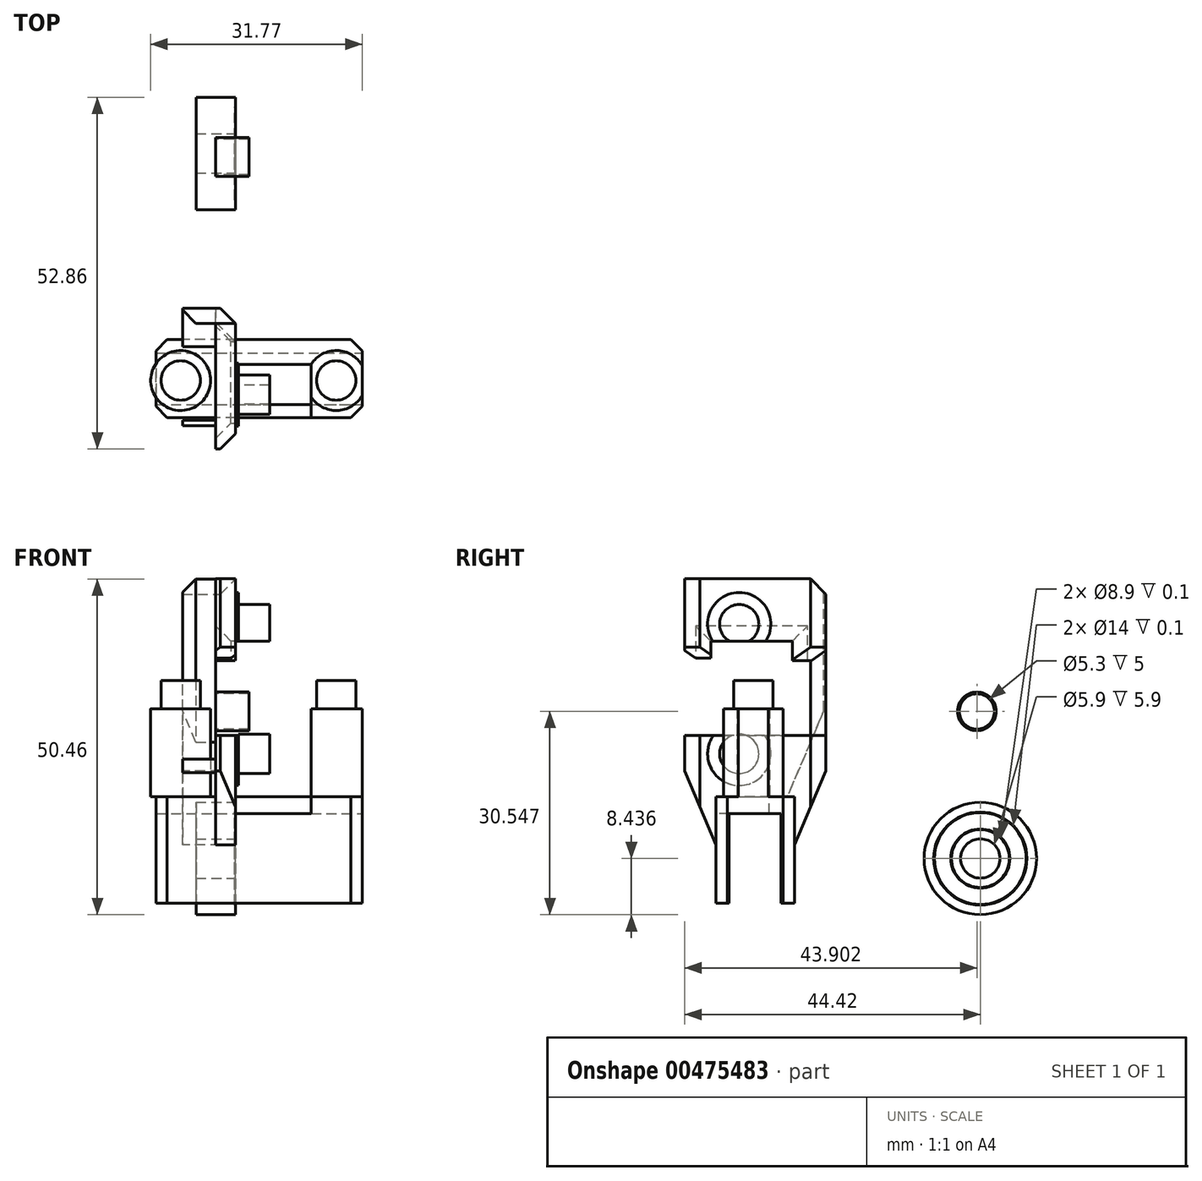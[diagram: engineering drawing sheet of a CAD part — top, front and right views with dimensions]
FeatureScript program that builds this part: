
annotation { "Feature Type Name" : "Feature", "Feature Type Description" : "" }
export const myFeature = defineFeature(function(context is Context, id is Id, definition is map)
    precondition{}
    {
        {
            var Q0;
            Q0=qCreatedBy(makeId("Right.planeOp"),FACE);
            var sketch = newSketch(context, id + "F0", { "sketchPlane" : qUnion([Q0])});
            skLineSegment(sketch, "E0", {"start": v(16.47, 8.85) * mm, "end": v(16.47, -7.15) * mm});
            skLineSegment(sketch, "E1", {"start": v(16.47, -7.15) * mm, "end": v(14.47, -7.15) * mm});
            skLineSegment(sketch, "E2", {"start": v(14.47, -7.15) * mm, "end": v(14.47, 6.35) * mm});
            skLineSegment(sketch, "E3", {"start": v(6.67, 6.35) * mm, "end": v(6.67, -7.15) * mm});
            skLineSegment(sketch, "E4", {"start": v(4.71, -7.15) * mm, "end": v(4.71, 8.85) * mm});
            skLineSegment(sketch, "E5", {"start": v(4.71, 8.85) * mm, "end": v(16.47, 8.85) * mm});
            skLineSegment(sketch, "E6.trimOffspring", {"start": v(14.47, 6.35) * mm, "end": v(6.67, 6.35) * mm});
            skLineSegment(sketch, "E7.trimOffspring", {"start": v(6.67, -7.15) * mm, "end": v(4.71, -7.15) * mm});
            skCircle(sketch, "E8", {"center": v(44.42, -0.43) * mm, "radius": 8.44 * mm});
            skCircle(sketch, "E9", {"center": v(44.42, -0.43) * mm, "radius": 2.95 * mm});
            skLineSegment(sketch, "E10", {"start": v(0, 41.6) * mm, "end": v(21.19, 41.6) * mm});
            skLineSegment(sketch, "E11", {"start": v(3.93, 21.47) * mm, "end": v(16.17, 21.47) * mm});
            skLineSegment(sketch, "E12", {"start": v(16.17, 21.47) * mm, "end": v(16.17, 32.21) * mm});
            skLineSegment(sketch, "E13", {"start": v(0, 41.6) * mm, "end": v(0, 12.74) * mm});
            skLineSegment(sketch, "E14", {"start": v(3.93, 32.21) * mm, "end": v(3.93, 21.47) * mm});
            skLineSegment(sketch, "E15", {"start": v(0, 12.74) * mm, "end": v(4.71, 1.64) * mm});
            skCircle(sketch, "E16", {"center": v(44.42, -0.43) * mm, "radius": 4.35 * mm});
            skCircle(sketch, "E17", {"center": v(44.42, -0.43) * mm, "radius": 4.45 * mm});
            skCircle(sketch, "E18", {"center": v(44.42, -0.43) * mm, "radius": 7 * mm});
            skCircle(sketch, "E19", {"center": v(44.42, -0.43) * mm, "radius": 6.9 * mm});
            skLineSegment(sketch, "E20", {"start": v(3.93, 32.21) * mm, "end": v(16.17, 32.21) * mm});
            skLineSegment(sketch, "E21", {"start": v(16.47, 1.64) * mm, "end": v(21.19, 12.74) * mm});
            skLineSegment(sketch, "E22", {"start": v(21.19, 12.74) * mm, "end": v(21.19, 41.6) * mm});
            skCircle(sketch, "E23.0", {"center": v(8.2, 15.3) * mm, "radius": 2.95 * mm});
            skArc(sketch, "E23.1", {"start": v(9.6, 32.21) * mm, "mid": v(8.2, 37.75) * mm, "end": v(6.78, 32.21) * mm});
            skArc(sketch, "E24", {"start": v(12.17, 32.21) * mm, "mid": v(8.2, 39.55) * mm, "end": v(4.2, 32.21) * mm});
            skArc(sketch, "E25", {"start": v(3.5, 14.5) * mm, "mid": v(12.87, 16.1) * mm, "end": v(3.5, 14.51) * mm});
            skLineSegment(sketch, "E26", {"start": v(1.75, 41.6) * mm, "end": v(1.75, 18.64) * mm});
            skLineSegment(sketch, "E27", {"start": v(18.9, 41.6) * mm, "end": v(18.9, 17.06) * mm});
            skLineSegment(sketch, "E28", {"start": v(18.9, 17.06) * mm, "end": v(15.4, 8.85) * mm});
            skLineSegment(sketch, "E29", {"start": v(1.75, 18.64) * mm, "end": v(5.91, 8.85) * mm});
            skCircle(sketch, "E30", {"center": v(43.9, 21.68) * mm, "radius": 2.65 * mm});
            skCircle(sketch, "E31", {"center": v(43.9, 21.68) * mm, "radius": 2.9 * mm});
            skLineSegment(sketch, "E32", {"start": v(3.5, 14.51) * mm, "end": v(3.5, 14.5) * mm});
            skSolve(sketch);
        }
        {
            var Q0;
            Q0=makeQuery(id+"F0.imprint","IMPRINT",FACE,{"disambiguationData":[TD([[makeQuery(id+"F0.imprint","IMPRINT",EDGE,{"derivedFrom":sQuery(id+"F0.wireOp",EDGE,"E0")}),-1.0]])]});
            extrude(context, id + "F1", {"entities" : qUnion([Q0]), "oppositeDirection" : true, "depth" : 9 * mm, "offsetDistance" : 25 * mm});
        }
        {
            var Q0;
            Q0=makeQuery(id+"F0.imprint","IMPRINT",FACE,{"disambiguationData":[TD([[makeQuery(id+"F0.imprint","IMPRINT",EDGE,{"derivedFrom":sQuery(id+"F0.wireOp",EDGE,"E0")}),-1.0]])]});
            extrude(context, id + "F2", {"entities" : qUnion([Q0]), "operationType" : NewBodyOperationType.ADD, "depth" : 22 * mm, "offsetDistance" : 25 * mm});
        }
        {
            var Q0;
            Q0=makeQuery(id+"F0.imprint","IMPRINT",FACE,{"disambiguationData":[TD([[makeQuery(id+"F0.imprint","IMPRINT",EDGE,{"derivedFrom":sQuery(id+"F0.wireOp",EDGE,"E4")}),1.0]])]});
            var Q1;
            {var subQ0=sQuery(id+"F0.wireOp",EDGE,"E24");Q1=makeQuery(id+"F0.imprint","IMPRINT",FACE,{"disambiguationData":[TD([[makeQuery(id+"F0.imprint","IMPRINT",EDGE,{"derivedFrom":subQ0}),1.0]])]});}
            var Q2;
            Q2=makeQuery(id+"F0.imprint","IMPRINT",FACE,{"disambiguationData":[TD([[makeQuery(id+"F0.imprint","IMPRINT",EDGE,{"derivedFrom":sQuery(id+"F0.wireOp",EDGE,"E23.0")}),-1.0]])]});
            var Q3;
            {var subQ5=sQuery(id+"F0.wireOp",EDGE,"N7SW8Tvq-peLj-d8hC-b9Bx-wYODAvh42Vg8");Q3=makeQuery(id+"F0.imprint","IMPRINT",FACE,{"disambiguationData":[TD([[makeQuery(id+"F0.imprint","IMPRINT",EDGE,{"derivedFrom":subQ5}),1.0]])]});}
            var Q4;
            {var subQ5=sQuery(id+"F0.wireOp",EDGE,"2wB0xuDN-6za4-80fk-EIJ2-dwkkp9VSf7dO");Q4=makeQuery(id+"F0.imprint","IMPRINT",FACE,{"disambiguationData":[TD([[makeQuery(id+"F0.imprint","IMPRINT",EDGE,{"derivedFrom":subQ5}),-1.0]])]});}
            var Q5;
            {var subQ3=sQuery(id+"F0.wireOp",EDGE,"1ilUMg3S-6E9J-L5an-a0RG-rZSRoxiEg0z6");Q5=makeQuery(id+"F0.imprint","IMPRINT",FACE,{"disambiguationData":[TD([[makeQuery(id+"F0.imprint","IMPRINT",EDGE,{"derivedFrom":subQ3}),1.0]])]});}
            var Q6;
            {var subQ5=sQuery(id+"F0.wireOp",EDGE,"BMftJzpG-nXOZ-MVrK-hpTt-UoZ4K3T9nTGc");Q6=makeQuery(id+"F0.imprint","IMPRINT",FACE,{"disambiguationData":[TD([[makeQuery(id+"F0.imprint","IMPRINT",EDGE,{"derivedFrom":subQ5}),-1.0]])]});}
            var Q7;
            {var subQ0=sQuery(id+"F0.wireOp",EDGE,"E22");Q7=makeQuery(id+"F0.imprint","IMPRINT",FACE,{"disambiguationData":[TD([[makeQuery(id+"F0.imprint","IMPRINT",EDGE,{"derivedFrom":subQ0}),1.0]])]});}
            var Q8;
            {var subQ0=sQuery(id+"F0.wireOp",EDGE,"E13");Q8=makeQuery(id+"F0.imprint","IMPRINT",FACE,{"disambiguationData":[TD([[makeQuery(id+"F0.imprint","IMPRINT",EDGE,{"derivedFrom":subQ0}),1.0]])]});}
            var Q9;
            Q9=makeQuery(id+"F0.imprint","IMPRINT",FACE,{"disambiguationData":[TD([[makeQuery(id+"F0.imprint","IMPRINT",EDGE,{"derivedFrom":sQuery(id+"F0.wireOp",EDGE,"E11")}),-1.0]])]});
            var Q10;
            {var subQ0=sQuery(id+"F0.wireOp",EDGE,"E32");Q10=makeQuery(id+"F0.imprint","IMPRINT",FACE,{"disambiguationData":[TD([[makeQuery(id+"F0.imprint","IMPRINT",EDGE,{"derivedFrom":subQ0}),1.0]])]});}
            extrude(context, id + "F3", {"entities" : qUnion([Q0, Q1, Q2, Q3, Q4, Q5, Q6, Q7, Q8, Q9, Q10]), "operationType" : NewBodyOperationType.ADD, "depth" : 3 * mm, "offsetDistance" : 25 * mm});
        }
        {
            var Q0;
            {var subQ0=sQuery(id+"F0.wireOp",EDGE,"E13");Q0=makeQuery(id+"F0.imprint","IMPRINT",FACE,{"disambiguationData":[TD([[makeQuery(id+"F0.imprint","IMPRINT",EDGE,{"derivedFrom":subQ0}),1.0]])]});}
            var Q1;
            {var subQ0=sQuery(id+"F0.wireOp",EDGE,"E22");Q1=makeQuery(id+"F0.imprint","IMPRINT",FACE,{"disambiguationData":[TD([[makeQuery(id+"F0.imprint","IMPRINT",EDGE,{"derivedFrom":subQ0}),1.0]])]});}
            var Q2;
            {var subQ0=sQuery(id+"F0.wireOp",EDGE,"E32");Q2=makeQuery(id+"F0.imprint","IMPRINT",FACE,{"disambiguationData":[TD([[makeQuery(id+"F0.imprint","IMPRINT",EDGE,{"derivedFrom":subQ0}),1.0]])]});}
            extrude(context, id + "F4", {"entities" : qUnion([Q0, Q1, Q2]), "operationType" : NewBodyOperationType.ADD, "oppositeDirection" : true, "depth" : 5 * mm, "offsetDistance" : 25 * mm});
        }
        {
            var Q0;
            Q0=makeQuery(id+"F0.imprint","IMPRINT",FACE,{"disambiguationData":[TD([[makeQuery(id+"F0.imprint","IMPRINT",EDGE,{"derivedFrom":sQuery(id+"F0.wireOp",EDGE,"7a95fe76-a82b-47bc-b71d-d71758565e7d.1")}),1.0]])]});
            var Q1;
            Q1=makeQuery(id+"F0.imprint","IMPRINT",FACE,{"disambiguationData":[TD([[makeQuery(id+"F0.imprint","IMPRINT",EDGE,{"derivedFrom":sQuery(id+"F0.wireOp",EDGE,"4c5e037e-bfb9-4179-b28a-ed57e4a18d11.1")}),1.0]])]});
            var Q2;
            Q2=makeQuery(id+"F0.imprint","IMPRINT",FACE,{"disambiguationData":[TD([[makeQuery(id+"F0.imprint","IMPRINT",EDGE,{"derivedFrom":sQuery(id+"F0.wireOp",EDGE,"E23.0")}),1.0]])]});
            var Q3;
            {var subQ0=sQuery(id+"F0.wireOp",EDGE,"E23.1");Q3=makeQuery(id+"F0.imprint","IMPRINT",FACE,{"disambiguationData":[TD([[makeQuery(id+"F0.imprint","IMPRINT",EDGE,{"derivedFrom":subQ0}),1.0]])]});}
            extrude(context, id + "F5", {"entities" : qUnion([Q0, Q1, Q2, Q3]), "operationType" : NewBodyOperationType.ADD, "depth" : 8.1 * mm, "offsetDistance" : 25 * mm});
        }
        {
            var Q0;
            {var subQ0=sQuery(id+"F0.wireOp",EDGE,"E24");Q0=makeQuery(id+"F0.imprint","IMPRINT",FACE,{"disambiguationData":[TD([[makeQuery(id+"F0.imprint","IMPRINT",EDGE,{"derivedFrom":subQ0}),1.0]])]});}
            var Q1;
            Q1=makeQuery(id+"F0.imprint","IMPRINT",FACE,{"disambiguationData":[TD([[makeQuery(id+"F0.imprint","IMPRINT",EDGE,{"derivedFrom":sQuery(id+"F0.wireOp",EDGE,"E23.0")}),-1.0]])]});
            var Q2;
            {var subQ0=sQuery(id+"F0.wireOp",EDGE,"E32");Q2=makeQuery(id+"F0.imprint","IMPRINT",FACE,{"disambiguationData":[TD([[makeQuery(id+"F0.imprint","IMPRINT",EDGE,{"derivedFrom":subQ0}),1.0]])]});}
            extrude(context, id + "F6", {"entities" : qUnion([Q0, Q1, Q2]), "operationType" : NewBodyOperationType.ADD, "depth" : 3.4 * mm, "offsetDistance" : 25 * mm});
        }
        {
            var Q0;
            {var subQ0=sQuery(id+"F0.wireOp",EDGE,"E0");var subQ1=sQuery(id+"F0.wireOp",EDGE,"E4");var subQ3=sQuery(id+"F0.wireOp",EDGE,"E5");Q0=makeQuery(id+"F3.boolean.opBoolean","SPLIT",FACE,{"disambiguationData":[TD([makeQuery(id+"F1.opExtrude","CAP_FACE",FACE,{"disambiguationData":[OSD([subQ0,sQuery(id+"F0.wireOp",EDGE,"E1"),sQuery(id+"F0.wireOp",EDGE,"E2"),sQuery(id+"F0.wireOp",EDGE,"E3"),subQ1,subQ3,sQuery(id+"F0.wireOp",EDGE,"E6.trimOffspring"),sQuery(id+"F0.wireOp",EDGE,"E7.trimOffspring")])],"isStart":false})])],"derivedFrom":makeQuery(id+"F2.boolean.opBoolean","MERGE",FACE,{"derivedFrom":[makeQuery(id+"F1.opExtrude","SWEPT_FACE",FACE,{"disambiguationData":[OSD([subQ3])]}),makeQuery(id+"F2.opExtrude","SWEPT_FACE",FACE,{"disambiguationData":[OSD([subQ3])]})]})});}
            var sketch = newSketch(context, id + "F7", { "sketchPlane" : qUnion([Q0])});
            skCircle(sketch, "E33.0", {"center": v(-5.27, 10.3) * mm, "radius": 2.96 * mm});
            skCircle(sketch, "E33.1", {"center": v(18.1, 10.3) * mm, "radius": 2.96 * mm});
            skCircle(sketch, "E34", {"center": v(-5.27, 10.3) * mm, "radius": 4.5 * mm});
            skArc(sketch, "E35", {"start": v(22, 12.55) * mm, "mid": v(13.6, 10.3) * mm, "end": v(22, 8.07) * mm});
            skLineSegment(sketch, "E36.0", {"start": v(22, 8.07) * mm, "end": v(22, 12.55) * mm});
            skPoint(sketch, "E37.orphan", {"position": v(22, 16.47) * mm});
            skPoint(sketch, "E38.orphan", {"position": v(22, 4.71) * mm});
            skSolve(sketch);
        }
        {
            var Q0;
            {var subQ0=sQuery(id+"F7.wireOp",EDGE,"006e9b06-de1a-4e6b-b88b-39552be878e9.0");var subQ1=sQuery(id+"F0.wireOp",EDGE,"E4");var subQ2=sQuery(id+"F0.wireOp",EDGE,"E5");var subQ3=makeQuery(id+"F3.boolean.opBoolean","SPLIT",EDGE,{"disambiguationData":[TD([makeQuery(id+"F1.opExtrude","CAP_FACE",FACE,{"disambiguationData":[OSD([sQuery(id+"F0.wireOp",EDGE,"E0"),sQuery(id+"F0.wireOp",EDGE,"E1"),sQuery(id+"F0.wireOp",EDGE,"E2"),sQuery(id+"F0.wireOp",EDGE,"E3"),subQ1,subQ2,sQuery(id+"F0.wireOp",EDGE,"E6.trimOffspring"),sQuery(id+"F0.wireOp",EDGE,"E7.trimOffspring")])],"isStart":false})])],"derivedFrom":makeQuery(id+"F2.boolean.opBoolean","MERGE",EDGE,{"derivedFrom":[makeQuery(id+"F1.opExtrude","SWEPT_EDGE",EDGE,{"disambiguationData":[OSD([subQ1,subQ2])]}),makeQuery(id+"F2.opExtrude","SWEPT_EDGE",EDGE,{"disambiguationData":[OSD([subQ1,subQ2])]})]})});var subQ4=makeQuery(id+"F7.imprint","INTERSECT",VERTEX,{"disambiguationData":[OD(0.0)],"derivedFrom":[subQ3,subQ0]});Q0=makeQuery(id+"F7.imprint","IMPRINT",FACE,{"disambiguationData":[TD([[makeQuery(id+"F7.imprint","IMPRINT",EDGE,{"disambiguationData":[TD([[subQ4,-1.0]])],"derivedFrom":subQ0}),-1.0]])]});}
            var Q1;
            {var subQ0=sQuery(id+"F7.wireOp",EDGE,"scUp9ceF-Qq33-h5mQ-G7V0-FORdipvKPfS7");var subQ1=sQuery(id+"F7.wireOp",EDGE,"006e9b06-de1a-4e6b-b88b-39552be878e9.0");var subQ2=makeQuery(id+"F7.imprint","INTERSECT",VERTEX,{"disambiguationData":[OD(0.0)],"derivedFrom":[subQ1,subQ0]});Q1=makeQuery(id+"F7.imprint","IMPRINT",FACE,{"disambiguationData":[TD([[makeQuery(id+"F7.imprint","IMPRINT",EDGE,{"disambiguationData":[TD([[subQ2,-1.0]])],"derivedFrom":subQ0}),1.0]])]});}
            var Q2;
            Q2=makeQuery(id+"F7.imprint","IMPRINT",FACE,{"disambiguationData":[TD([[makeQuery(id+"F7.imprint","IMPRINT",EDGE,{"derivedFrom":sQuery(id+"F7.wireOp",EDGE,"006e9b06-de1a-4e6b-b88b-39552be878e9.1")}),-1.0]])]});
            var Q3;
            Q3=makeQuery(id+"F7.imprint","IMPRINT",FACE,{"disambiguationData":[TD([[makeQuery(id+"F7.imprint","IMPRINT",EDGE,{"derivedFrom":sQuery(id+"F7.wireOp",EDGE,"E33.0")}),1.0]])]});
            var Q4;
            Q4=makeQuery(id+"F7.imprint","IMPRINT",FACE,{"disambiguationData":[TD([[makeQuery(id+"F7.imprint","IMPRINT",EDGE,{"derivedFrom":sQuery(id+"F7.wireOp",EDGE,"E33.1")}),1.0]])]});
            extrude(context, id + "F8", {"entities" : qUnion([Q0, Q1, Q2, Q3, Q4]), "operationType" : NewBodyOperationType.ADD, "depth" : 17.5 * mm, "offsetDistance" : 25 * mm});
        }
        {
            var Q0;
            {var subQ0=sQuery(id+"F7.wireOp",EDGE,"scUp9ceF-Qq33-h5mQ-G7V0-FORdipvKPfS7");var subQ1=sQuery(id+"F7.wireOp",EDGE,"006e9b06-de1a-4e6b-b88b-39552be878e9.0");var subQ2=makeQuery(id+"F7.imprint","INTERSECT",VERTEX,{"disambiguationData":[OD(1.0)],"derivedFrom":[subQ1,subQ0]});Q0=makeQuery(id+"F7.imprint","IMPRINT",FACE,{"disambiguationData":[TD([[makeQuery(id+"F7.imprint","IMPRINT",EDGE,{"disambiguationData":[TD([[subQ2,-1.0]])],"derivedFrom":subQ0}),1.0]])]});}
            var Q1;
            {var subQ0=sQuery(id+"F7.wireOp",EDGE,"scUp9ceF-Qq33-h5mQ-G7V0-FORdipvKPfS7");var subQ1=sQuery(id+"F7.wireOp",EDGE,"006e9b06-de1a-4e6b-b88b-39552be878e9.0");var subQ2=makeQuery(id+"F7.imprint","INTERSECT",VERTEX,{"disambiguationData":[OD(0.0)],"derivedFrom":[subQ1,subQ0]});Q1=makeQuery(id+"F7.imprint","IMPRINT",FACE,{"disambiguationData":[TD([[makeQuery(id+"F7.imprint","IMPRINT",EDGE,{"disambiguationData":[TD([[subQ2,1.0]])],"derivedFrom":subQ0}),1.0]])]});}
            var Q2;
            {var subQ0=sQuery(id+"F7.wireOp",EDGE,"006e9b06-de1a-4e6b-b88b-39552be878e9.0");var subQ1=sQuery(id+"F0.wireOp",EDGE,"E4");var subQ2=sQuery(id+"F0.wireOp",EDGE,"E5");var subQ3=makeQuery(id+"F3.boolean.opBoolean","SPLIT",EDGE,{"disambiguationData":[TD([makeQuery(id+"F1.opExtrude","CAP_FACE",FACE,{"disambiguationData":[OSD([sQuery(id+"F0.wireOp",EDGE,"E0"),sQuery(id+"F0.wireOp",EDGE,"E1"),sQuery(id+"F0.wireOp",EDGE,"E2"),sQuery(id+"F0.wireOp",EDGE,"E3"),subQ1,subQ2,sQuery(id+"F0.wireOp",EDGE,"E6.trimOffspring"),sQuery(id+"F0.wireOp",EDGE,"E7.trimOffspring")])],"isStart":false})])],"derivedFrom":makeQuery(id+"F2.boolean.opBoolean","MERGE",EDGE,{"derivedFrom":[makeQuery(id+"F1.opExtrude","SWEPT_EDGE",EDGE,{"disambiguationData":[OSD([subQ1,subQ2])]}),makeQuery(id+"F2.opExtrude","SWEPT_EDGE",EDGE,{"disambiguationData":[OSD([subQ1,subQ2])]})]})});var subQ4=makeQuery(id+"F7.imprint","INTERSECT",VERTEX,{"disambiguationData":[OD(0.0)],"derivedFrom":[subQ3,subQ0]});Q2=makeQuery(id+"F7.imprint","IMPRINT",FACE,{"disambiguationData":[TD([[makeQuery(id+"F7.imprint","IMPRINT",EDGE,{"disambiguationData":[TD([[subQ4,-1.0]])],"derivedFrom":subQ0}),1.0]])]});}
            var Q3;
            Q3=makeQuery(id+"F7.imprint","IMPRINT",FACE,{"disambiguationData":[TD([[makeQuery(id+"F7.imprint","IMPRINT",EDGE,{"derivedFrom":sQuery(id+"F7.wireOp",EDGE,"006e9b06-de1a-4e6b-b88b-39552be878e9.1")}),1.0]])]});
            var Q4;
            Q4=makeQuery(id+"F7.imprint","IMPRINT",FACE,{"disambiguationData":[TD([[makeQuery(id+"F7.imprint","IMPRINT",EDGE,{"derivedFrom":sQuery(id+"F7.wireOp",EDGE,"E33.0")}),-1.0]])]});
            var Q5;
            Q5=makeQuery(id+"F7.imprint","IMPRINT",FACE,{"disambiguationData":[TD([[makeQuery(id+"F7.imprint","IMPRINT",EDGE,{"derivedFrom":sQuery(id+"F7.wireOp",EDGE,"E33.1")}),-1.0]])]});
            var Q6;
            {var subQ0=sQuery(id+"F7.wireOp",EDGE,"E34");var subQ1=sQuery(id+"F0.wireOp",EDGE,"E5");var subQ2=sQuery(id+"F0.wireOp",EDGE,"E29");var subQ5=makeQuery(id+"F4.opExtrude","SWEPT_EDGE",EDGE,{"disambiguationData":[OSD([subQ1,subQ2])]});var subQ6=makeQuery(id+"F7.imprint","INTERSECT",VERTEX,{"derivedFrom":[subQ5,subQ0]});Q6=makeQuery(id+"F7.imprint","IMPRINT",FACE,{"disambiguationData":[TD([[makeQuery(id+"F7.imprint","IMPRINT",EDGE,{"disambiguationData":[TD([[subQ6,1.0]])],"derivedFrom":subQ0}),1.0]])]});}
            extrude(context, id + "F9", {"entities" : qUnion([Q0, Q1, Q2, Q3, Q4, Q5, Q6]), "operationType" : NewBodyOperationType.ADD, "depth" : 13.23 * mm, "offsetDistance" : 25 * mm});
        }
        {
            var Q0;
            {var subQ0=sQuery(id+"F0.wireOp",EDGE,"E5");var subQ1=sQuery(id+"F0.wireOp",EDGE,"E7.trimOffspring");var subQ2=sQuery(id+"F0.wireOp",EDGE,"E4");Q0=makeQuery(id+"F3.boolean.opBoolean","SPLIT",FACE,{"disambiguationData":[TD([makeQuery(id+"F2.opExtrude","CAP_FACE",FACE,{"disambiguationData":[OSD([sQuery(id+"F0.wireOp",EDGE,"E0"),sQuery(id+"F0.wireOp",EDGE,"E1"),sQuery(id+"F0.wireOp",EDGE,"E2"),sQuery(id+"F0.wireOp",EDGE,"E3"),subQ2,subQ0,sQuery(id+"F0.wireOp",EDGE,"E6.trimOffspring"),subQ1])],"isStart":false})])],"derivedFrom":makeQuery(id+"F2.boolean.opBoolean","MERGE",FACE,{"derivedFrom":[makeQuery(id+"F1.opExtrude","SWEPT_FACE",FACE,{"disambiguationData":[OSD([subQ2])]}),makeQuery(id+"F2.opExtrude","SWEPT_FACE",FACE,{"disambiguationData":[OSD([subQ2])]})]})});}
            var sketch = newSketch(context, id + "F10", { "sketchPlane" : qUnion([Q0])});
            skLineSegment(sketch, "E39", {"start": v(3, 8.85) * mm, "end": v(3, 6.34) * mm});
            skLineSegment(sketch, "E40", {"start": v(3, 6.34) * mm, "end": v(14.33, 6.34) * mm});
            skLineSegment(sketch, "E41", {"start": v(14.33, 6.34) * mm, "end": v(14.33, 8.85) * mm});
            skLineSegment(sketch, "E42", {"start": v(14.33, 8.85) * mm, "end": v(3, 8.85) * mm});
            skPoint(sketch, "E43.0", {"position": v(3, 41.6) * mm});
            skLineSegment(sketch, "E44.bottom", {"start": v(0, 29.33) * mm, "end": v(3.44, 29.33) * mm});
            skLineSegment(sketch, "E44.top", {"start": v(0, 18.05) * mm, "end": v(3.44, 18.05) * mm});
            skLineSegment(sketch, "E44.left", {"start": v(0, 29.33) * mm, "end": v(0, 18.05) * mm});
            skLineSegment(sketch, "E44.right", {"start": v(3.44, 29.33) * mm, "end": v(3.44, 18.05) * mm});
            skLineSegment(sketch, "E45.bottom", {"start": v(12.56, 23.46) * mm, "end": v(14.33, 23.46) * mm});
            skLineSegment(sketch, "E45.top", {"start": v(12.56, 8.85) * mm, "end": v(14.33, 8.85) * mm});
            skLineSegment(sketch, "E45.left", {"start": v(12.56, 23.46) * mm, "end": v(12.56, 8.85) * mm});
            skLineSegment(sketch, "E45.right", {"start": v(14.33, 23.46) * mm, "end": v(14.33, 8.85) * mm});
            skSolve(sketch);
        }
        {
            var Q0;
            Q0=makeQuery(id+"F10.imprint","IMPRINT",FACE,{"disambiguationData":[TD([[makeQuery(id+"F10.imprint","IMPRINT",EDGE,{"derivedFrom":sQuery(id+"F10.wireOp",EDGE,"E39")}),-1.0]])]});
            extrude(context, id + "F11", {"entities" : qUnion([Q0]), "operationType" : NewBodyOperationType.REMOVE, "oppositeDirection" : true, "depth" : 8 * mm, "offsetDistance" : 25 * mm});
        }
        {
            var Q0;
            Q0=makeQuery(id+"F10.imprint","IMPRINT",FACE,{"disambiguationData":[TD([[makeQuery(id+"F10.imprint","IMPRINT",EDGE,{"derivedFrom":sQuery(id+"F10.wireOp",EDGE,"E44.bottom")}),-1.0]])]});
            var Q1;
            Q1=makeQuery(id+"F10.imprint","IMPRINT",FACE,{"disambiguationData":[TD([[makeQuery(id+"F10.imprint","IMPRINT",EDGE,{"derivedFrom":sQuery(id+"F10.wireOp",EDGE,"E45.bottom")}),-1.0]])]});
            extrude(context, id + "F12", {"entities" : qUnion([Q0, Q1]), "operationType" : NewBodyOperationType.REMOVE, "oppositeDirection" : true, "depth" : 35 * mm, "offsetDistance" : 25 * mm, "symmetric" : true});
        }
        {
            var Q0;
            Q0=makeQuery(id+"F3.opExtrude","CAP_EDGE",EDGE,{"disambiguationData":[OSD([sQuery(id+"F0.wireOp",EDGE,"E12")])],"isStart":true});
            var Q1;
            Q1=makeQuery(id+"F3.opExtrude","CAP_EDGE",EDGE,{"disambiguationData":[OSD([sQuery(id+"F0.wireOp",EDGE,"lIxJYqOd-Sp0v-Uxvu-6HAH-ZMBPeLFcKROz")])],"isStart":true});
            var Q2;
            Q2=makeQuery(id+"F3.opExtrude","CAP_EDGE",EDGE,{"disambiguationData":[OSD([sQuery(id+"F0.wireOp",EDGE,"E13")])],"isStart":false});
            var Q3;
            {var subQ0=sQuery(id+"F0.wireOp",EDGE,"E20");var subQ1=sQuery(id+"F0.wireOp",EDGE,"E24");var subQ2=makeQuery(id+"F0.imprint","INTERSECT",VERTEX,{"disambiguationData":[OD(0.0)],"derivedFrom":[subQ0,subQ1]});var subQ4=makeQuery(id+"F0.imprint","INTERSECT",VERTEX,{"disambiguationData":[OD(1.0)],"derivedFrom":[subQ0,subQ1]});Q3=makeQuery(id+"F5.boolean.opBoolean","MERGE",EDGE,{"derivedFrom":[makeQuery(id+"F3.opExtrude","CAP_EDGE",EDGE,{"disambiguationData":[OSD([subQ0]),TDD([makeQuery(id+"F0.imprint","IMPRINT",EDGE,{"disambiguationData":[TD([[makeQuery(id+"F0.imprint","INTERSECT",VERTEX,{"derivedFrom":[sQuery(id+"F0.wireOp",EDGE,"E14"),subQ0]}),-1.0]])],"derivedFrom":subQ0}),makeQuery(id+"F0.imprint","IMPRINT",EDGE,{"disambiguationData":[TD([[subQ4,-1.0]])],"derivedFrom":subQ0})])],"isStart":true}),makeQuery(id+"F3.opExtrude","CAP_EDGE",EDGE,{"disambiguationData":[OSD([subQ0]),TDD([makeQuery(id+"F0.imprint","IMPRINT",EDGE,{"disambiguationData":[TD([[subQ2,1.0]])],"derivedFrom":subQ0}),makeQuery(id+"F0.imprint","IMPRINT",EDGE,{"disambiguationData":[TD([[makeQuery(id+"F0.imprint","INTERSECT",VERTEX,{"derivedFrom":[sQuery(id+"F0.wireOp",EDGE,"E12"),subQ0]}),1.0]])],"derivedFrom":subQ0})])],"isStart":true}),makeQuery(id+"F5.opExtrude","CAP_EDGE",EDGE,{"disambiguationData":[OSD([subQ0])],"isStart":true})]});}
            var Q4;
            Q4=makeQuery(id+"F3.opExtrude","CAP_EDGE",EDGE,{"disambiguationData":[OSD([sQuery(id+"F0.wireOp",EDGE,"E14")])],"isStart":true});
            var Q5;
            Q5=makeQuery(id+"F3.opExtrude","CAP_EDGE",EDGE,{"disambiguationData":[OSD([sQuery(id+"F0.wireOp",EDGE,"E22")])],"isStart":false});
            var Q6;
            Q6=makeQuery(id+"F3.opExtrude","CAP_EDGE",EDGE,{"disambiguationData":[OSD([sQuery(id+"F0.wireOp",EDGE,"E0")])],"isStart":true});
            var Q7;
            Q7=makeQuery(id+"F3.opExtrude","CAP_EDGE",EDGE,{"disambiguationData":[OSD([sQuery(id+"F0.wireOp",EDGE,"E0")])],"isStart":false});
            var Q8;
            Q8=makeQuery(id+"F3.opExtrude","CAP_EDGE",EDGE,{"disambiguationData":[OSD([sQuery(id+"F0.wireOp",EDGE,"E5")])],"isStart":true});
            var Q9;
            Q9=makeQuery(id+"F3.opExtrude","CAP_EDGE",EDGE,{"disambiguationData":[OSD([sQuery(id+"F0.wireOp",EDGE,"E4")])],"isStart":true});
            var Q10;
            Q10=makeQuery(id+"F4.opExtrude","CAP_EDGE",EDGE,{"disambiguationData":[OSD([sQuery(id+"F0.wireOp",EDGE,"E0")])],"isStart":false});
            var Q11;
            Q11=makeQuery(id+"F4.opExtrude","CAP_EDGE",EDGE,{"disambiguationData":[OSD([sQuery(id+"F0.wireOp",EDGE,"E4")])],"isStart":false});
            var Q12;
            {var subQ0=sQuery(id+"F0.wireOp",EDGE,"E5");Q12=makeQuery(id+"F4.opExtrude","CAP_EDGE",EDGE,{"disambiguationData":[OSD([subQ0]),TDD([makeQuery(id+"F0.imprint","IMPRINT",EDGE,{"disambiguationData":[TD([[makeQuery(id+"F0.imprint","INTERSECT",VERTEX,{"derivedFrom":[sQuery(id+"F0.wireOp",EDGE,"E0"),subQ0]}),1.0]])],"derivedFrom":subQ0})])],"isStart":false});}
            var Q13;
            {var subQ0=sQuery(id+"F0.wireOp",EDGE,"E13");var subQ1=sQuery(id+"F0.wireOp",EDGE,"E10");Q13=makeQuery(id+"F4.boolean.opBoolean","MERGE",EDGE,{"derivedFrom":[makeQuery(id+"F3.opExtrude","SWEPT_EDGE",EDGE,{"disambiguationData":[OSD([subQ1,subQ0])]}),makeQuery(id+"F4.opExtrude","SWEPT_EDGE",EDGE,{"disambiguationData":[OSD([subQ1,subQ0])]})]});}
            var Q14;
            {var subQ0=sQuery(id+"F0.wireOp",EDGE,"E22");var subQ1=sQuery(id+"F0.wireOp",EDGE,"E10");Q14=makeQuery(id+"F4.boolean.opBoolean","MERGE",EDGE,{"derivedFrom":[makeQuery(id+"F3.opExtrude","SWEPT_EDGE",EDGE,{"disambiguationData":[OSD([subQ1,subQ0])]}),makeQuery(id+"F4.opExtrude","SWEPT_EDGE",EDGE,{"disambiguationData":[OSD([subQ1,subQ0])]})]});}
            var Q15;
            Q15=makeQuery(id+"F12.boolean.opBoolean","INTERSECT",EDGE,{"derivedFrom":[makeQuery(id+"F11.boolean.opBoolean","COPY",FACE,{"derivedFrom":makeQuery(id+"F11.opExtrude","CAP_FACE",FACE,{"disambiguationData":[OSD([sQuery(id+"F10.wireOp",EDGE,"E39"),sQuery(id+"F10.wireOp",EDGE,"E40"),sQuery(id+"F10.wireOp",EDGE,"E41"),sQuery(id+"F10.wireOp",EDGE,"E42"),sQuery(id+"F10.wireOp",EDGE,"E45.bottom"),sQuery(id+"F10.wireOp",EDGE,"E45.left"),sQuery(id+"F10.wireOp",EDGE,"E45.right")])],"isStart":false})}),makeQuery(id+"F12.opExtrude","SWEPT_FACE",FACE,{"disambiguationData":[OSD([sQuery(id+"F10.wireOp",EDGE,"E45.top")])]})]});
            chamfer(context, id + "F13", {"entities" : qUnion([Q0, Q1, Q2, Q3, Q4, Q5, Q6, Q7, Q8, Q9, Q10, Q11, Q12, Q13, Q14, Q15]), "width" : 2.3 * mm, "tangentPropagation" : true});
        }
        {
            var Q0;
            Q0=makeQuery(id+"F4.opExtrude","CAP_EDGE",EDGE,{"disambiguationData":[OSD([sQuery(id+"F0.wireOp",EDGE,"E27")])],"isStart":false});
            var Q1;
            Q1=makeQuery(id+"F4.opExtrude","CAP_EDGE",EDGE,{"disambiguationData":[OSD([sQuery(id+"F0.wireOp",EDGE,"E26")])],"isStart":false});
            var Q2;
            {var subQ0=sQuery(id+"F10.wireOp",EDGE,"E44.top");var subQ1=makeQuery(id+"F12.opExtrude","SWEPT_FACE",FACE,{"disambiguationData":[OSD([subQ0])]});var subQ2=makeQuery(id+"F11.boolean.opBoolean","COPY",FACE,{"derivedFrom":makeQuery(id+"F11.opExtrude","SWEPT_FACE",FACE,{"disambiguationData":[OSD([subQ0])]})});var subQ3=sQuery(id+"F0.wireOp",EDGE,"E15");var subQ4=sQuery(id+"F0.wireOp",EDGE,"E13");Q2=makeQuery(id+"F13.opChamfer","BLEND_EDGE",EDGE,{"blendedFrom":[makeQuery(id+"F12.boolean.opBoolean","SPLIT",EDGE,{"disambiguationData":[TD([makeQuery(id+"F3.opExtrude","SWEPT_FACE",FACE,{"disambiguationData":[OSD([subQ3])]})])],"derivedFrom":makeQuery(id+"F3.opExtrude","CAP_EDGE",EDGE,{"disambiguationData":[OSD([subQ4])],"isStart":false})}),makeQuery(id+"F12.boolean.opBoolean","MERGE",FACE,{"derivedFrom":[subQ2],"fromTools":[subQ1]})],"blendedInto":[makeQuery(id+"F12.boolean.opBoolean","MERGE",FACE,{"derivedFrom":[subQ2],"fromTools":[subQ1]})]});}
            var Q3;
            {var subQ0=sQuery(id+"F10.wireOp",EDGE,"E44.top");var subQ1=makeQuery(id+"F12.opExtrude","SWEPT_FACE",FACE,{"disambiguationData":[OSD([subQ0])]});var subQ2=makeQuery(id+"F11.boolean.opBoolean","COPY",FACE,{"derivedFrom":makeQuery(id+"F11.opExtrude","SWEPT_FACE",FACE,{"disambiguationData":[OSD([subQ0])]})});var subQ3=sQuery(id+"F0.wireOp",EDGE,"E21");var subQ4=sQuery(id+"F0.wireOp",EDGE,"E22");Q3=makeQuery(id+"F13.opChamfer","BLEND_EDGE",EDGE,{"blendedFrom":[makeQuery(id+"F12.boolean.opBoolean","SPLIT",EDGE,{"disambiguationData":[TD([makeQuery(id+"F3.opExtrude","SWEPT_FACE",FACE,{"disambiguationData":[OSD([subQ3])]})])],"derivedFrom":makeQuery(id+"F3.opExtrude","CAP_EDGE",EDGE,{"disambiguationData":[OSD([subQ4])],"isStart":false})}),makeQuery(id+"F12.boolean.opBoolean","MERGE",FACE,{"derivedFrom":[subQ2],"fromTools":[subQ1]})],"blendedInto":[makeQuery(id+"F12.boolean.opBoolean","MERGE",FACE,{"derivedFrom":[subQ2],"fromTools":[subQ1]})]});}
            var Q4;
            {var subQ0=sQuery(id+"F0.wireOp",EDGE,"E22");var subQ2=sQuery(id+"F0.wireOp",EDGE,"E12");var subQ11=sQuery(id+"F0.wireOp",EDGE,"E10");var subQ18=makeQuery(id+"F12.opExtrude","SWEPT_FACE",FACE,{"disambiguationData":[OSD([sQuery(id+"F10.wireOp",EDGE,"E44.bottom")])]});Q4=makeQuery(id+"F13.opChamfer","BLEND_EDGE",EDGE,{"blendedFrom":[makeQuery(id+"F12.boolean.opBoolean","SPLIT",EDGE,{"disambiguationData":[TD([makeQuery(id+"F3.opExtrude","SWEPT_FACE",FACE,{"disambiguationData":[OSD([subQ11])]})])],"derivedFrom":makeQuery(id+"F3.opExtrude","CAP_EDGE",EDGE,{"disambiguationData":[OSD([subQ0])],"isStart":false})}),makeQuery(id+"F12.boolean.opBoolean","COPY",FACE,{"disambiguationData":[TD([makeQuery(id+"F3.opExtrude","SWEPT_FACE",FACE,{"disambiguationData":[OSD([subQ2])]})])],"derivedFrom":subQ18})],"blendedInto":[makeQuery(id+"F12.boolean.opBoolean","COPY",FACE,{"disambiguationData":[TD([makeQuery(id+"F3.opExtrude","SWEPT_FACE",FACE,{"disambiguationData":[OSD([subQ2])]})])],"derivedFrom":subQ18})]});}
            var Q5;
            {var subQ2=sQuery(id+"F0.wireOp",EDGE,"E13");var subQ3=makeQuery(id+"F3.opExtrude","SWEPT_FACE",FACE,{"disambiguationData":[OSD([subQ2])]});var subQ11=sQuery(id+"F0.wireOp",EDGE,"E10");var subQ18=makeQuery(id+"F12.opExtrude","SWEPT_FACE",FACE,{"disambiguationData":[OSD([sQuery(id+"F10.wireOp",EDGE,"E44.bottom")])]});Q5=makeQuery(id+"F13.opChamfer","BLEND_EDGE",EDGE,{"blendedFrom":[makeQuery(id+"F12.boolean.opBoolean","SPLIT",EDGE,{"disambiguationData":[TD([makeQuery(id+"F3.opExtrude","SWEPT_FACE",FACE,{"disambiguationData":[OSD([subQ11])]})])],"derivedFrom":makeQuery(id+"F3.opExtrude","CAP_EDGE",EDGE,{"disambiguationData":[OSD([subQ2])],"isStart":false})}),makeQuery(id+"F12.boolean.opBoolean","COPY",FACE,{"disambiguationData":[TD([subQ3])],"derivedFrom":subQ18})],"blendedInto":[makeQuery(id+"F12.boolean.opBoolean","COPY",FACE,{"disambiguationData":[TD([subQ3])],"derivedFrom":subQ18})]});}
            var Q6;
            {var subQ1=sQuery(id+"F0.wireOp",EDGE,"E23.0");var subQ3=sQuery(id+"F0.wireOp",EDGE,"E26");Q6=makeQuery(id+"F12.boolean.opBoolean","SPLIT",EDGE,{"disambiguationData":[topologyDisambiguationEdgeConnected([makeQuery(id+"F5.opExtrude","CAP_FACE",FACE,{"disambiguationData":[OSD([subQ1])],"isStart":true})])],"derivedFrom":makeQuery(id+"F4.opExtrude","CAP_EDGE",EDGE,{"disambiguationData":[OSD([subQ3])],"isStart":true})});}
            var Q7;
            {var subQ0=sQuery(id+"F0.wireOp",EDGE,"E13");var subQ1=sQuery(id+"F0.wireOp",EDGE,"E10");var subQ2=sQuery(id+"F0.wireOp",EDGE,"E22");var subQ3=sQuery(id+"F0.wireOp",EDGE,"E27");var subQ4=sQuery(id+"F0.wireOp",EDGE,"E23.1");var subQ5=sQuery(id+"F0.wireOp",EDGE,"E20");var subQ6=makeQuery(id+"F5.opExtrude","CAP_FACE",FACE,{"disambiguationData":[OSD([subQ5,subQ4])],"isStart":true});var subQ7=sQuery(id+"F0.wireOp",EDGE,"E23.0");var subQ8=makeQuery(id+"F3.opExtrude","CAP_FACE",FACE,{"disambiguationData":[OSD([sQuery(id+"F0.wireOp",EDGE,"E0"),sQuery(id+"F0.wireOp",EDGE,"E4"),sQuery(id+"F0.wireOp",EDGE,"E5"),subQ1,sQuery(id+"F0.wireOp",EDGE,"E11"),sQuery(id+"F0.wireOp",EDGE,"E12"),subQ0,sQuery(id+"F0.wireOp",EDGE,"E14"),sQuery(id+"F0.wireOp",EDGE,"E15"),subQ5,sQuery(id+"F0.wireOp",EDGE,"E21"),subQ2,subQ7,subQ4])],"isStart":true});var subQ9=makeQuery(id+"F4.opExtrude","SWEPT_FACE",FACE,{"disambiguationData":[OSD([subQ3])]});var subQ10=makeQuery(id+"F5.opExtrude","CAP_FACE",FACE,{"disambiguationData":[OSD([subQ7])],"isStart":true});Q7=makeQuery(id+"F12.boolean.opBoolean","SPLIT",EDGE,{"disambiguationData":[topologyDisambiguationEdgeConnected([subQ8,subQ9,subQ6,subQ10]),TD([makeQuery(id+"F3.opExtrude","SWEPT_FACE",FACE,{"disambiguationData":[OSD([subQ1])]})])],"derivedFrom":makeQuery(id+"F4.opExtrude","CAP_EDGE",EDGE,{"disambiguationData":[OSD([subQ3])],"isStart":true})});}
            var Q8;
            {var subQ0=sQuery(id+"F0.wireOp",EDGE,"E5");var subQ1=sQuery(id+"F10.wireOp",EDGE,"E45.top");var subQ2=sQuery(id+"F10.wireOp",EDGE,"E42");var subQ4=makeQuery(id+"F11.opExtrude","CAP_EDGE",EDGE,{"disambiguationData":[OSD([subQ2,subQ1])],"isStart":false});Q8=makeQuery(id+"F12.boolean.opBoolean","MERGE",EDGE,{"derivedFrom":[makeQuery(id+"F11.boolean.opBoolean","COPY",EDGE,{"disambiguationData":[topologyDisambiguationEdgeConnected([makeQuery(id+"F11.opExtrude","SWEPT_FACE",FACE,{"disambiguationData":[OSD([subQ2,subQ1])]})])],"derivedFrom":subQ4}),makeQuery(id+"F11.boolean.opBoolean","COPY",EDGE,{"disambiguationData":[topologyDisambiguationEdgeConnected([makeQuery(id+"F1.opExtrude","SWEPT_FACE",FACE,{"disambiguationData":[OSD([subQ0])]})])],"derivedFrom":subQ4})]});}
            chamfer(context, id + "F14", {"entities" : qUnion([Q0, Q1, Q2, Q3, Q4, Q5, Q6, Q7, Q8]), "width" : 2 * mm, "tangentPropagation" : true});
        }
        {
            var Q0;
            Q0=makeQuery(id+"F0.imprint","IMPRINT",FACE,{"disambiguationData":[TD([[makeQuery(id+"F0.imprint","IMPRINT",EDGE,{"derivedFrom":sQuery(id+"F0.wireOp",EDGE,"E16")}),-1.0]])]});
            var Q1;
            Q1=makeQuery(id+"F0.imprint","IMPRINT",FACE,{"disambiguationData":[TD([[makeQuery(id+"F0.imprint","IMPRINT",EDGE,{"derivedFrom":sQuery(id+"F0.wireOp",EDGE,"E18")}),1.0]])]});
            extrude(context, id + "F15", {"entities" : qUnion([Q0, Q1]), "depth" : 5.7 * mm, "offsetDistance" : 25 * mm, "symmetric" : true});
        }
        {
            var Q0;
            Q0=makeQuery(id+"F1.opExtrude","CAP_FACE",FACE,{"disambiguationData":[OSD([sQuery(id+"F0.wireOp",EDGE,"E8"),sQuery(id+"F0.wireOp",EDGE,"E9")])],"isStart":true});
            var Q1;
            Q1=makeQuery(id+"F0.imprint","IMPRINT",FACE,{"disambiguationData":[TD([[makeQuery(id+"F0.imprint","IMPRINT",EDGE,{"derivedFrom":sQuery(id+"F0.wireOp",EDGE,"E8")}),1.0]])]});
            var Q2;
            Q2=makeQuery(id+"F0.imprint","IMPRINT",FACE,{"disambiguationData":[TD([[makeQuery(id+"F0.imprint","IMPRINT",EDGE,{"derivedFrom":sQuery(id+"F0.wireOp",EDGE,"E9")}),-1.0]])]});
            var Q3;
            Q3=makeQuery(id+"F0.imprint","IMPRINT",FACE,{"disambiguationData":[TD([[makeQuery(id+"F0.imprint","IMPRINT",EDGE,{"derivedFrom":sQuery(id+"F0.wireOp",EDGE,"E17")}),-1.0]])]});
            extrude(context, id + "F16", {"entities" : qUnion([Q0, Q1, Q2, Q3]), "operationType" : NewBodyOperationType.ADD, "oppositeDirection" : true, "depth" : 5.9 * mm, "offsetDistance" : 25 * mm, "symmetric" : true});
        }
        {
            var Q0;
            Q0=makeQuery(id+"F0.imprint","IMPRINT",FACE,{"disambiguationData":[TD([[makeQuery(id+"F0.imprint","IMPRINT",EDGE,{"derivedFrom":sQuery(id+"F0.wireOp",EDGE,"E30")}),-1.0]])]});
            extrude(context, id + "F17", {"entities" : qUnion([Q0]), "depth" : 5 * mm, "offsetDistance" : 25 * mm});
        }
        {
            var Q0;
            Q0=makeQuery(id+"F2.opExtrude","CAP_EDGE",EDGE,{"disambiguationData":[OSD([sQuery(id+"F0.wireOp",EDGE,"E4")])],"isStart":false});
            var Q1;
            Q1=makeQuery(id+"F2.opExtrude","CAP_EDGE",EDGE,{"disambiguationData":[OSD([sQuery(id+"F0.wireOp",EDGE,"E0")])],"isStart":false});
            var Q2;
            Q2=makeQuery(id+"F1.opExtrude","CAP_EDGE",EDGE,{"disambiguationData":[OSD([sQuery(id+"F0.wireOp",EDGE,"E4")])],"isStart":false});
            var Q3;
            Q3=makeQuery(id+"F1.opExtrude","CAP_EDGE",EDGE,{"disambiguationData":[OSD([sQuery(id+"F0.wireOp",EDGE,"E0")])],"isStart":false});
            chamfer(context, id + "F18", {"entities" : qUnion([Q0, Q1, Q2, Q3]), "width" : 1.7 * mm, "tangentPropagation" : true});
        }
    });
